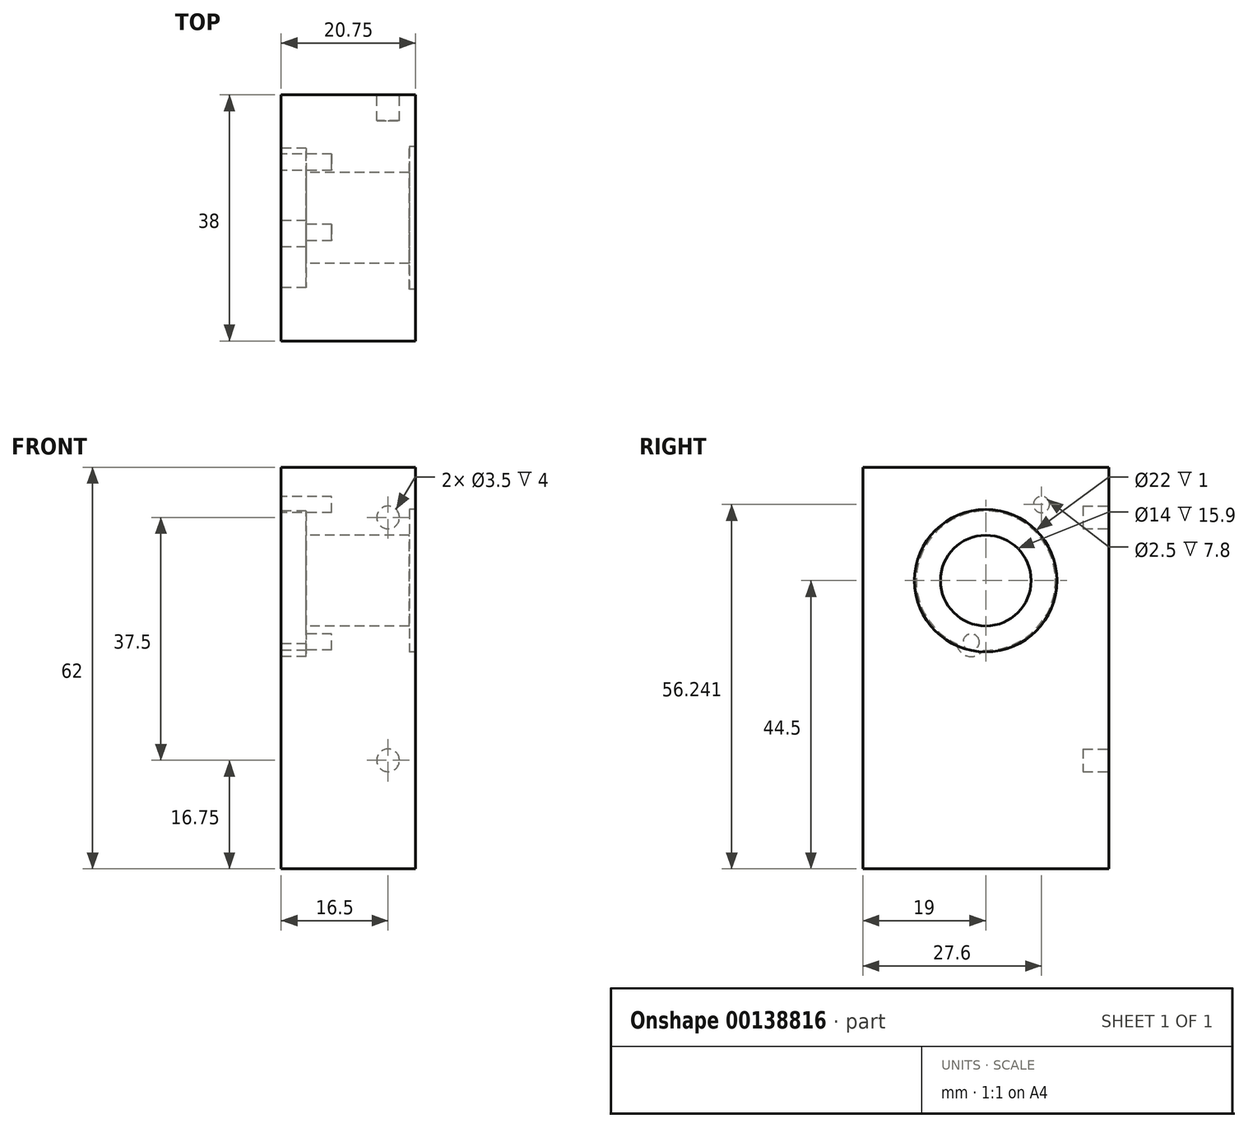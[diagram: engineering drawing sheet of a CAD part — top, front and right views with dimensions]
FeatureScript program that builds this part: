
annotation { "Feature Type Name" : "Feature", "Feature Type Description" : "" }
export const myFeature = defineFeature(function(context is Context, id is Id, definition is map)
    precondition{}
    {
        {
            var Q0;
            Q0=qCreatedBy(makeId("Right.planeOp"),FACE);
            var sketch = newSketch(context, id + "F0", { "sketchPlane" : qUnion([Q0])});
            skLineSegment(sketch, "E0.bottom", {"start": v(-19, -31) * mm, "end": v(19, -31) * mm});
            skLineSegment(sketch, "E0.top", {"start": v(-19, 31) * mm, "end": v(19, 31) * mm});
            skLineSegment(sketch, "E0.left", {"start": v(-19, -31) * mm, "end": v(-19, 31) * mm});
            skLineSegment(sketch, "E0.right", {"start": v(19, -31) * mm, "end": v(19, 31) * mm});
            skPoint(sketch, "E0.middle", {"position": v(0, 0) * mm});
            skSolve(sketch);
        }
        {
            var Q0;
            Q0=qSketchRegion(id+"F0",true);
            extrude(context, id + "F1", {"entities" : qUnion([Q0]), "depth" : 20.75 * mm});
        }
        {
            var Q0;
            Q0=makeQuery(id+"F1.opExtrude","CAP_FACE",FACE,{"disambiguationData":[OSD([sQuery(id+"F0.wireOp",EDGE,"E0.bottom"),sQuery(id+"F0.wireOp",EDGE,"E0.top"),sQuery(id+"F0.wireOp",EDGE,"E0.left"),sQuery(id+"F0.wireOp",EDGE,"E0.right")])],"isStart":false});
            var sketch = newSketch(context, id + "F2", { "sketchPlane" : qUnion([Q0])});
            skLineSegment(sketch, "E1", {"start": v(0, 31) * mm, "end": v(0, -31) * mm, "construction": true});
            skCircle(sketch, "E2", {"center": v(0, 13.5) * mm, "radius": 7 * mm});
            skArc(sketch, "E3", {"start": v(-0.38, 2.76) * mm, "mid": v(2.48, 23.96) * mm, "end": v(-4.48, 3.73) * mm});
            skLineSegment(sketch, "E4", {"start": v(0, 24) * mm, "end": v(8.6, 24) * mm, "construction": true});
            skCircle(sketch, "E5", {"center": v(8.6, 25.24) * mm, "radius": 1.25 * mm});
            skCircle(sketch, "E6", {"center": v(-2.25, 4.01) * mm, "radius": 1.25 * mm});
            skArc(sketch, "E7.0", {"start": v(-4.48, 3.73) * mm, "mid": v(-2.77, 1.82) * mm, "end": v(-0.38, 2.76) * mm});
            skSolve(sketch);
        }
        {
            var Q0;
            Q0=makeQuery(id+"F2.imprint","IMPRINT",FACE,{"disambiguationData":[TD([[makeQuery(id+"F2.imprint","IMPRINT",EDGE,{"derivedFrom":sQuery(id+"F2.wireOp",EDGE,"E2")}),-1.0]])]});
            extrude(context, id + "F3", {"entities" : qUnion([Q0]), "operationType" : NewBodyOperationType.REMOVE, "oppositeDirection" : true, "depth" : 3.85 * mm});
        }
        {
            var Q0;
            Q0=makeQuery(id+"F2.imprint","IMPRINT",FACE,{"disambiguationData":[TD([[makeQuery(id+"F2.imprint","IMPRINT",EDGE,{"derivedFrom":sQuery(id+"F2.wireOp",EDGE,"E6")}),1.0]])]});
            var Q1;
            Q1=makeQuery(id+"F2.imprint","IMPRINT",FACE,{"disambiguationData":[TD([[makeQuery(id+"F2.imprint","IMPRINT",EDGE,{"derivedFrom":sQuery(id+"F2.wireOp",EDGE,"E5")}),1.0]])]});
            extrude(context, id + "F4", {"entities" : qUnion([Q0, Q1]), "operationType" : NewBodyOperationType.REMOVE, "oppositeDirection" : true, "depth" : 7.8 * mm});
        }
        {
            var Q0;
            Q0=makeQuery(id+"F2.imprint","IMPRINT",FACE,{"disambiguationData":[TD([[makeQuery(id+"F2.imprint","IMPRINT",EDGE,{"derivedFrom":sQuery(id+"F2.wireOp",EDGE,"E2")}),1.0]])]});
            extrude(context, id + "F5", {"entities" : qUnion([Q0]), "operationType" : NewBodyOperationType.REMOVE, "endBound" : BoundingType.THROUGH_ALL, "oppositeDirection" : true, "depth" : 25 * mm});
        }
        {
            var Q0;
            Q0=makeQuery(id+"F1.opExtrude","CAP_FACE",FACE,{"disambiguationData":[OSD([sQuery(id+"F0.wireOp",EDGE,"E0.bottom"),sQuery(id+"F0.wireOp",EDGE,"E0.top"),sQuery(id+"F0.wireOp",EDGE,"E0.left"),sQuery(id+"F0.wireOp",EDGE,"E0.right")])],"isStart":true});
            var sketch = newSketch(context, id + "F6", { "sketchPlane" : qUnion([Q0])});
            skCircle(sketch, "E8", {"center": v(0, 13.5) * mm, "radius": 11 * mm});
            skSolve(sketch);
        }
        {
            var Q0;
            Q0=makeQuery(id+"F6.imprint","IMPRINT",FACE,{"disambiguationData":[TD([[makeQuery(id+"F6.imprint","IMPRINT",EDGE,{"derivedFrom":sQuery(id+"F6.wireOp",EDGE,"E8")}),1.0]])]});
            extrude(context, id + "F7", {"entities" : qUnion([Q0]), "operationType" : NewBodyOperationType.REMOVE, "oppositeDirection" : true, "depth" : 1 * mm});
        }
        {
            var Q0;
            Q0=makeQuery(id+"F1.opExtrude","SWEPT_BODY",BODY,{"disambiguationData":[OSD([sQuery(id+"F0.wireOp",EDGE,"E0.bottom"),sQuery(id+"F0.wireOp",EDGE,"E0.top"),sQuery(id+"F0.wireOp",EDGE,"E0.left"),sQuery(id+"F0.wireOp",EDGE,"E0.right")])]});
            var Q1;
            Q1=qCreatedBy(makeId("Right.planeOp"),FACE);
            mirror(context, id + "F8", {"operationType" : NewBodyOperationType.ADD, "entities" : qUnion([Q0]), "mirrorPlane" : qUnion([Q1])});
        }
        {
            var Q0;
            {var subQ0=makeQuery(id+"F1.opExtrude","SWEPT_FACE",FACE,{"disambiguationData":[OSD([sQuery(id+"F0.wireOp",EDGE,"E0.left")])]});Q0=makeQuery(id+"F8.boolean.opBoolean","MERGE",FACE,{"derivedFrom":[subQ0,makeQuery(id+"F8.opPattern","COPY",FACE,{"derivedFrom":subQ0,"instanceName":"1"})]});}
            var sketch = newSketch(context, id + "F9", { "sketchPlane" : qUnion([Q0])});
            skLineSegment(sketch, "E9", {"start": v(0, 31) * mm, "end": v(0, -31) * mm});
            skLineSegment(sketch, "E10", {"start": v(0, -31) * mm, "end": v(20.75, -31) * mm});
            skLineSegment(sketch, "E11", {"start": v(20.75, -31) * mm, "end": v(20.75, 31) * mm});
            skLineSegment(sketch, "E12", {"start": v(20.75, 31) * mm, "end": v(0, 31) * mm});
            skSolve(sketch);
        }
        {
            var Q0;
            Q0 = qSketchRegion(id + "F9", true);
            extrude(context, id + "F10", {"entities" : qUnion([Q0]), "operationType" : NewBodyOperationType.REMOVE, "endBound" : BoundingType.THROUGH_ALL, "oppositeDirection" : true, "depth" : 25 * mm});
        }
        {
            var Q0;
            {var subQ0=makeQuery(id+"F1.opExtrude","SWEPT_FACE",FACE,{"disambiguationData":[OSD([sQuery(id+"F0.wireOp",EDGE,"E0.right")])]});Q0=makeQuery(id+"F8.boolean.opBoolean","MERGE",FACE,{"derivedFrom":[subQ0,makeQuery(id+"F8.opPattern","COPY",FACE,{"derivedFrom":subQ0,"instanceName":"1"})]});}
            var sketch = newSketch(context, id + "F11", { "sketchPlane" : qUnion([Q0])});
            skCircle(sketch, "E13", {"center": v(4.25, 23.25) * mm, "radius": 1.75 * mm});
            skCircle(sketch, "E14", {"center": v(4.25, -14.25) * mm, "radius": 1.75 * mm});
            skSolve(sketch);
        }
        {
            var Q0;
            Q0 = qSketchRegion(id + "F11", true);
            extrude(context, id + "F12", {"entities" : qUnion([Q0]), "operationType" : NewBodyOperationType.REMOVE, "oppositeDirection" : true, "depth" : 4 * mm});
        }
    });
